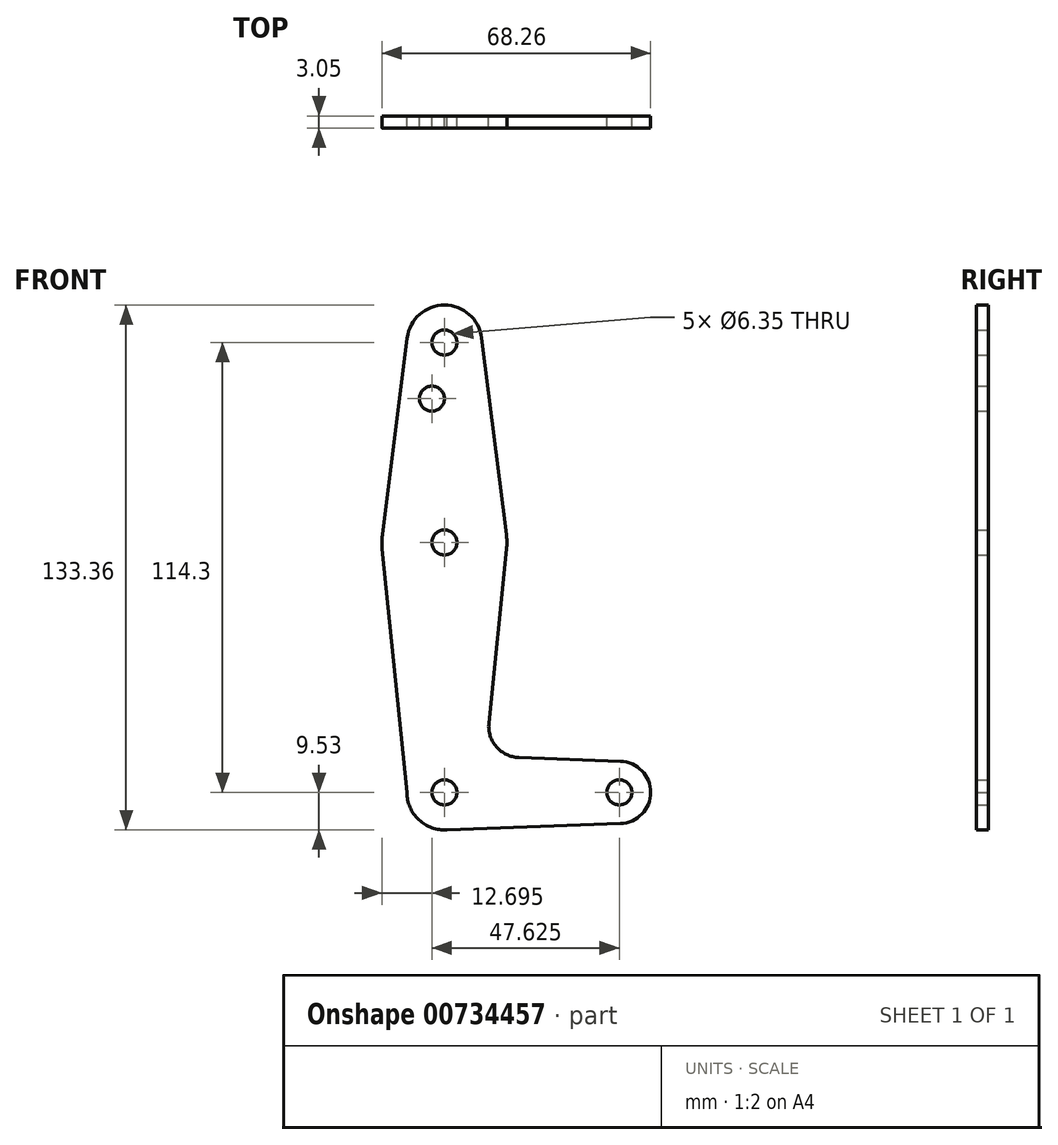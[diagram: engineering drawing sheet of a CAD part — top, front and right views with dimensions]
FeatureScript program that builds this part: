
annotation { "Feature Type Name" : "Feature", "Feature Type Description" : "" }
export const myFeature = defineFeature(function(context is Context, id is Id, definition is map)
    precondition{}
    {
        {
            var Q0;
            Q0=qCreatedBy(makeId("Front.planeOp"),FACE);
            var sketch = newSketch(context, id + "F0", { "sketchPlane" : qUnion([Q0])});
            skLineSegment(sketch, "E0", {"start": v(0, 114.3) * mm, "end": v(0, 0) * mm});
            skLineSegment(sketch, "E1", {"start": v(0, 0) * mm, "end": v(44.45, 0) * mm});
            skCircle(sketch, "E2", {"center": v(44.45, 0) * mm, "radius": 7.94 * mm});
            skCircle(sketch, "E3", {"center": v(0, 0) * mm, "radius": 9.53 * mm});
            skCircle(sketch, "E4", {"center": v(0, 63.5) * mm, "radius": 15.88 * mm});
            skCircle(sketch, "E5", {"center": v(0, 114.3) * mm, "radius": 9.53 * mm});
            skLineSegment(sketch, "E6", {"start": v(0, -9.53) * mm, "end": v(44.73, -7.93) * mm});
            skLineSegment(sketch, "E7", {"start": v(18.93, 8.85) * mm, "end": v(44.73, 7.93) * mm});
            skLineSegment(sketch, "E8", {"start": v(-9.53, 0) * mm, "end": v(-15.8, 61.9) * mm});
            skLineSegment(sketch, "E9", {"start": v(-9.45, 115.5) * mm, "end": v(-15.75, 65.48) * mm});
            skLineSegment(sketch, "E10", {"start": v(11.3, 17.6) * mm, "end": v(15.8, 61.9) * mm});
            skLineSegment(sketch, "E11", {"start": v(9.45, 115.5) * mm, "end": v(15.8, 65.14) * mm});
            skCircle(sketch, "E12", {"center": v(0, 114.3) * mm, "radius": 3.18 * mm});
            skCircle(sketch, "E13", {"center": v(0, 0) * mm, "radius": 3.18 * mm});
            skCircle(sketch, "E14", {"center": v(44.45, 0) * mm, "radius": 3.18 * mm});
            skCircle(sketch, "E15", {"center": v(0, 63.5) * mm, "radius": 3.18 * mm});
            skCircle(sketch, "E16", {"center": v(-3.18, 100.03) * mm, "radius": 3.18 * mm});
            skArc(sketch, "E17.filletArc", {"start": v(11.3, 17.6) * mm, "mid": v(13.22, 11.57) * mm, "end": v(18.93, 8.85) * mm});
            skSolve(sketch);
        }
        {
            var Q0;
            Q0 = qSketchRegion(id + "F0", true);
            var Q1;
            {var subQ0=sQuery(id+"F0.wireOp",EDGE,"E3");var subQ1=sQuery(id+"F0.wireOp",EDGE,"E0");var subQ2=makeQuery(id+"F0.imprint","INTERSECT",VERTEX,{"derivedFrom":[subQ1,subQ0]});Q1=makeQuery(id+"F0.imprint","IMPRINT",FACE,{"disambiguationData":[TD([[makeQuery(id+"F0.imprint","IMPRINT",EDGE,{"disambiguationData":[TD([[subQ2,-1.0]])],"derivedFrom":subQ1}),1.0]])]});}
            extrude(context, id + "F1", {"entities" : qUnion([Q0, Q1]), "depth" : 3.05 * mm, "offsetDistance" : 25.4 * mm});
        }
    });
